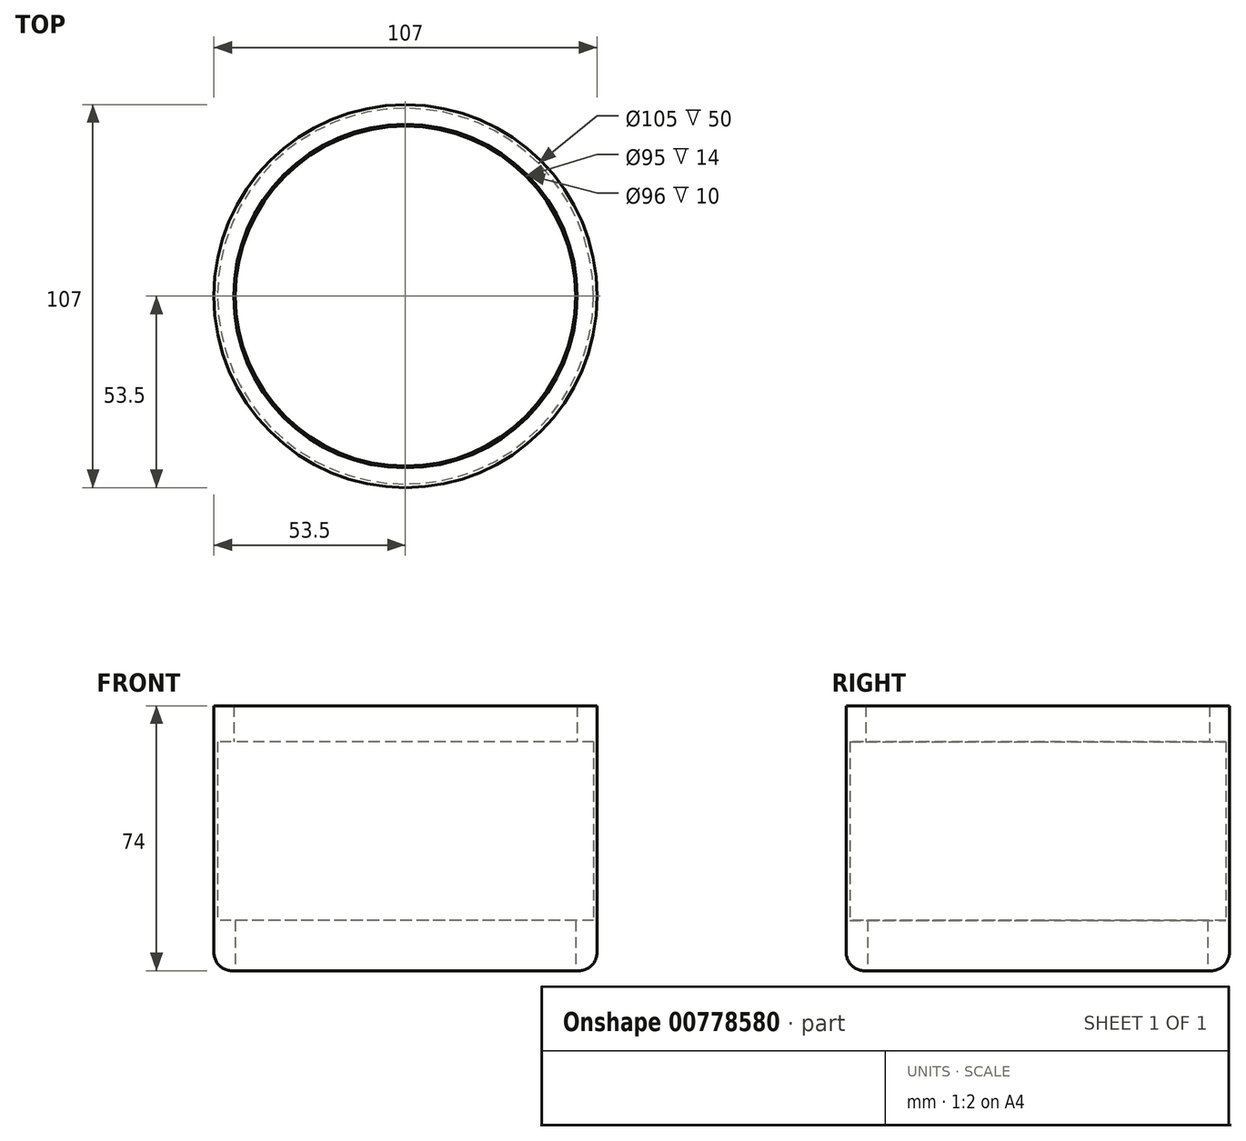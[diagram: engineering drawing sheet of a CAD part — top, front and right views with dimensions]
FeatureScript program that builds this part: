
annotation { "Feature Type Name" : "Feature", "Feature Type Description" : "" }
export const myFeature = defineFeature(function(context is Context, id is Id, definition is map)
    precondition{}
    {
        {
            var Q0;
            Q0=qCreatedBy(makeId("Top.planeOp"),FACE);
            var sketch = newSketch(context, id + "F0", { "sketchPlane" : qUnion([Q0])});
            skCircle(sketch, "E0", {"center": v(0, 0) * mm, "radius": 52.5 * mm});
            skCircle(sketch, "E1", {"center": v(0, 0) * mm, "radius": 47.5 * mm});
            skCircle(sketch, "E2", {"center": v(0, 0) * mm, "radius": 53.5 * mm});
            skCircle(sketch, "E3", {"center": v(0, 0) * mm, "radius": 50.5 * mm});
            skSolve(sketch);
        }
        {
            var Q0;
            Q0=makeQuery(id+"F0.imprint","IMPRINT",FACE,{"disambiguationData":[TD([[makeQuery(id+"F0.imprint","IMPRINT",EDGE,{"derivedFrom":sQuery(id+"F0.wireOp",EDGE,"E0")}),1.0]])]});
            var Q1;
            Q1=makeQuery(id+"F0.imprint","IMPRINT",FACE,{"disambiguationData":[TD([[makeQuery(id+"F0.imprint","IMPRINT",EDGE,{"derivedFrom":sQuery(id+"F0.wireOp",EDGE,"E1")}),-1.0]])]});
            extrude(context, id + "F1", {"entities" : qUnion([Q0, Q1]), "depth" : 10 * mm, "offsetDistance" : 25 * mm, "hasSecondDirection" : true, "secondDirectionOppositeDirection" : true, "secondDirectionDepth" : 4 * mm});
        }
        {
            var Q0;
            Q0=makeQuery(id+"F0.imprint","IMPRINT",FACE,{"disambiguationData":[TD([[makeQuery(id+"F0.imprint","IMPRINT",EDGE,{"derivedFrom":sQuery(id+"F0.wireOp",EDGE,"E0")}),-1.0]])]});
            extrude(context, id + "F2", {"entities" : qUnion([Q0]), "operationType" : NewBodyOperationType.ADD, "depth" : 70 * mm, "offsetDistance" : 25 * mm, "hasSecondDirection" : true, "secondDirectionOppositeDirection" : true, "secondDirectionDepth" : 4 * mm});
        }
        {
            var Q0;
            Q0=qCreatedBy(makeId("Top.planeOp"),FACE);
            cPlane(context, id + "F3", {"entities" : qUnion([Q0]), "cplaneType" : CPlaneType.OFFSET, "offset" : 60 * mm, "width" : 150 * mm, "height" : 150 * mm});
        }
        {
            var Q0;
            Q0=qCreatedBy(id+"F3.planeOp",FACE);
            var sketch = newSketch(context, id + "F4", { "sketchPlane" : qUnion([Q0])});
            skCircle(sketch, "E4", {"center": v(0, 0) * mm, "radius": 48 * mm});
            skCircle(sketch, "E5", {"center": v(0, 0) * mm, "radius": 52.5 * mm});
            skSolve(sketch);
        }
        {
            var Q0;
            Q0=makeQuery(id+"F4.imprint","IMPRINT",FACE,{"disambiguationData":[TD([[makeQuery(id+"F4.imprint","IMPRINT",EDGE,{"derivedFrom":sQuery(id+"F4.wireOp",EDGE,"E4")}),-1.0]])]});
            extrude(context, id + "F5", {"entities" : qUnion([Q0]), "operationType" : NewBodyOperationType.ADD, "depth" : 10 * mm, "offsetDistance" : 25 * mm});
        }
        {
            var Q0;
            Q0=qCreatedBy(id+"F3.planeOp",FACE);
            cPlane(context, id + "F6", {"entities" : qUnion([Q0]), "cplaneType" : CPlaneType.OFFSET, "offset" : 95 * mm, "width" : 150 * mm, "height" : 150 * mm});
        }
        {
            var Q0;
            Q0=qCreatedBy(id+"F6.planeOp",FACE);
            var sketch = newSketch(context, id + "F7", { "sketchPlane" : qUnion([Q0])});
            skCircle(sketch, "E6", {"center": v(0, 0) * mm, "radius": 45 * mm});
            skCircle(sketch, "E7", {"center": v(0, 0) * mm, "radius": 46 * mm});
            skSolve(sketch);
        }
        {
            var Q0;
            Q0=makeQuery(id+"F2.opExtrude","CAP_EDGE",EDGE,{"disambiguationData":[OSD([sQuery(id+"F0.wireOp",EDGE,"E2")])],"isStart":true});
            fillet(context, id + "F8", {"entities" : qUnion([Q0]), "radius" : 5 * mm, "tangentPropagation" : true, "allowEdgeOverflow" : false});
        }
        {
            var Q0;
            Q0=qCreatedBy(id+"F3.planeOp",FACE);
            cPlane(context, id + "F9", {"entities" : qUnion([Q0]), "cplaneType" : CPlaneType.OFFSET, "offset" : 30 * mm, "width" : 150 * mm, "height" : 150 * mm});
        }
        {
            var Q0;
            Q0=qCreatedBy(id+"F9.planeOp",FACE);
            var sketch = newSketch(context, id + "F10", { "sketchPlane" : qUnion([Q0])});
            skCircle(sketch, "E8", {"center": v(0, 0) * mm, "radius": 45 * mm});
            skCircle(sketch, "E9", {"center": v(0, 0) * mm, "radius": 44 * mm});
            skSolve(sketch);
        }
        {
            var Q0;
            Q0=qCreatedBy(id+"F9.planeOp",FACE);
            cPlane(context, id + "F11", {"entities" : qUnion([Q0]), "cplaneType" : CPlaneType.OFFSET, "offset" : 25 * mm, "width" : 150 * mm, "height" : 150 * mm});
        }
        {
            var Q0;
            Q0=qCreatedBy(id+"F11.planeOp",FACE);
            var sketch = newSketch(context, id + "F12", { "sketchPlane" : qUnion([Q0])});
            skCircle(sketch, "E10", {"center": v(0, 0) * mm, "radius": 51 * mm});
            skCircle(sketch, "E11", {"center": v(0, 0) * mm, "radius": 50 * mm});
            skSolve(sketch);
        }
        {
            var Q0;
            Q0=makeQuery(id+"F12.imprint","IMPRINT",FACE,{"disambiguationData":[TD([[makeQuery(id+"F12.imprint","IMPRINT",EDGE,{"derivedFrom":sQuery(id+"F12.wireOp",EDGE,"E11")}),1.0]])]});
            var Q1;
            Q1=makeQuery(id+"F10.imprint","IMPRINT",FACE,{"disambiguationData":[TD([[makeQuery(id+"F10.imprint","IMPRINT",EDGE,{"derivedFrom":sQuery(id+"F10.wireOp",EDGE,"E8")}),1.0]])]});
            var Q2;
            Q2=sQuery(id+"F7.wireOp",EDGE,"E6");
            var Q3;
            Q3=sQuery(id+"F12.wireOp",EDGE,"E10");
            var Q4;
            Q4=sQuery(id+"F10.wireOp",EDGE,"E8");
            var Q5;
            Q5=makeQuery(id+"F2.opExtrude","CAP_EDGE",EDGE,{"disambiguationData":[OSD([sQuery(id+"F0.wireOp",EDGE,"E2")])],"isStart":false});
            loft(context, id + "F13", {"bodyType" : ToolBodyType.SURFACE, "sheetProfilesArray" : [{ "sheetProfileEntities" : qUnion([Q0]) }, { "sheetProfileEntities" : qUnion([Q1]) }], "wireProfilesArray" : [{ "wireProfileEntities" : qUnion([Q2]) }, { "wireProfileEntities" : qUnion([Q3]) }, { "wireProfileEntities" : qUnion([Q4]) }, { "wireProfileEntities" : qUnion([Q5]) }]});
        }
        {
            var Q0;
            Q0=qCreatedBy(id+"F3.planeOp",FACE);
            cPlane(context, id + "F14", {"entities" : qUnion([Q0]), "cplaneType" : CPlaneType.OFFSET, "offset" : 10 * mm, "width" : 150 * mm, "height" : 150 * mm});
        }
    });
